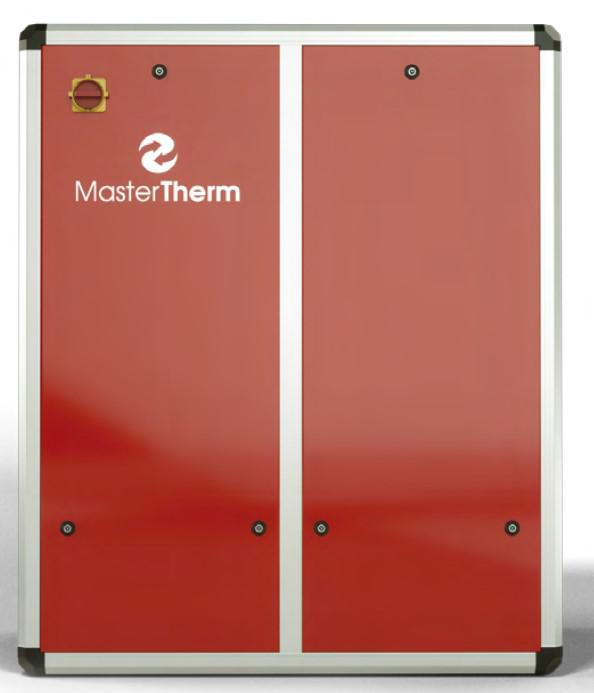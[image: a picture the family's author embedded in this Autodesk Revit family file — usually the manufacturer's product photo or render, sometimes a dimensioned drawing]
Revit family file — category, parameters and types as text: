
# Revit family: AQ-ZHX_ENG-RFA-2022
name_source: partatom
category: Mechanické zařízení
units: mm (PartAtom-declared; Revit-internal decimal feet)

## family parameters
Bod výpočtu místnosti = Ne
Kóta kulaté spojky = Použít průměr
Nadpis OmniClass = Climate Control (HVAC)
Ořezat dutým tvarem při načtení = Ne
Sdílené = Ne
Typ dílu = Normální
Vždy vertikální = Ano
Zachovat orientaci poznámky = Ne
Založené na pracovní rovině = Ne
Číslo OmniClass = 23.75.00.00

## types (5) — shared parameters
CI_condenser – inlet = 5/4'' (OD)
CO_condenser – outlet = 5/4'' (OD)
Desuperheater – inlet/outlet = not in unit
EI_evaporator – inlet = 5/4'' (OD)
EO_evaporator – outlet = 5/4'' (OD)
MT_CI diameter = 32 mm  [stored 0.104987 ft]
MT_CO diameter = 32 mm  [stored 0.104987 ft]
MT_EC1 offset_X = 25 mm  [stored 0.082021 ft]
MT_EC1 offset_Y = 90 mm  [stored 0.295276 ft]
MT_EC2 offset_X = 25 mm  [stored 0.082021 ft]
MT_EC2 offset_Y = 60 mm  [stored 0.19685 ft]
MT_EC3 offset_X = 25 mm  [stored 0.082021 ft]
MT_EC3 offset_Y = 30 mm  [stored 0.0984252 ft]
MT_EC4 offset_Y = 90 mm  [stored 0.295276 ft]
MT_EC5 offset_Y = 60 mm  [stored 0.19685 ft]
MT_EC6 offset_Y = 30 mm  [stored 0.0984252 ft]
MT_EC6_YES = Ano
MT_EI diameter = 32 mm  [stored 0.104987 ft]
MT_EO diameter = 32 mm  [stored 0.104987 ft]
MT_active power = 0 W
MT_angle length_Y = 596 mm  [stored 1.95538 ft]
MT_angle length_Z = 1080 mm
MT_angle offset = 60 mm  [stored 0.19685 ft]
MT_apparent power = 0 VA
MT_case depth = 716 mm  [stored 2.34908 ft]
MT_case height = 1200 mm
MT_case mat = MT_rgb161-42-32
MT_clearance back = 200 mm  [stored 0.656168 ft]
MT_clearance front = 600 mm
MT_clearance left = 400 mm  [stored 1.31234 ft]
MT_clearance right = 400 mm  [stored 1.31234 ft]
MT_clearance top = 1800 mm
MT_cover front_Y = 1120 mm
MT_cover side_X = 636 mm  [stored 2.08661 ft]
MT_cover side_Y = 1120 mm
MT_cover top_Y = 636 mm  [stored 2.08661 ft]
MT_desuperheater_YES = Ne
MT_frequency (Hz) = 50 Hz
MT_ground height = 30 mm  [stored 0.0984252 ft]
MT_pipe connector mat = MT_RGB-130-130-130
MT_pipe connector_Y = 120 mm  [stored 0.393701 ft]
MT_pipe mat = MT_angle-corner
MT_voltage (V) = 400 V
Popis = High-temperature heat pump
URL = https://www.mastertherm.eu
Výrobce = Master Therm
zero-valued in all types: Cena, MT_CosPhi, MT_desuperheater diameter, Výchozí výška

## per-type parameters (varying)
| type | El. connection | Komentáře k typům | MT_CI offset_X | MT_CO offset_X | MT_EC4 offset_X | MT_EC5 offset_X | MT_EC6 offset_X | MT_EI offset_X | MT_EO offset_X | MT_TYPE | MT_angle length_X | MT_case width | MT_center lock offset_H | MT_cover front_X | MT_cover top_X | MT_desuperheater offset_X | MT_double case_YES | MT_hmotnost (kg) | MT_lock offset_H | MT_logo offset_H | MT_max. current – compressor (A) | MT_pipe connector offset | MT_pipe connector_X | MT_power switch offset_H |
| AQ75ZHX | 4xPG16; 8xPG13.5 | COMPRESSOR: Scroll; 2900 rpm; charge of POE oil – 3.38 l; LRC – 174 (90); max. op. current – 35 A; EVAPORATOR: PHE; AISI316; water flow (W/W) – 3.04 kg/s; min. flow – 1.52 kg/s; temp. difference – 5 K; int. volume – 7.9 l; pump ext. head – 6.0 m; pump motor – 1100 W; CONDENSER: PHE; AISI316; water flow – 1.83 kg/s; min. flow – 1.83 kg/s; temp. difference – 10 K; int. volume – 6.9 l; pump ext. head – 5.0 m; pump motor – 310 W; REFRIGERANT CIRCUIT: R134a (5.0 kg); AUX. HEATER (optional); CONTROLS: controller – pCO5; EEV – yes; water probe – yes; SHW probe/output – yes (2x); mixing probe/output – yes; outdoor probe – yes; dynamic set point – yes; refrigerant probe – 2xPT; POWER SUPPLY: 3x400 V; 50 Hz; max. current – 40 A; max. current, incl. aux. heater – on demand; DIMENSIONS: hot water, brine – 5/4", 5/4" (OD); 120x101x72 cm; 400 kg; LIMITS: max. water overpress. – 0.25 MPa; max. refr. overpress. – 2.9 MPa; brine min./max.: 0/45 °C; water min./max.: 20/80 °C | 73 mm  [stored 0.239501 ft] | 173 mm  [stored 0.567585 ft] | 907 mm | 907 mm | 907 mm | 759 mm  [stored 2.49016 ft] | 859 mm  [stored 2.81824 ft] | 75 | 892 mm  [stored 2.92651 ft] | 1012 mm | 263 mm  [stored 0.862861 ft] | 932 mm | 932 mm | 466 mm  [stored 1.52887 ft] | Ano | 400 | 100 mm  [stored 0.328084 ft] | 263 mm  [stored 0.862861 ft] | 40 A | 972 mm | 932 mm | 175 mm  [stored 0.574147 ft] |
| AQ60ZHX | 2xPG21; 2xPG16; 4xPG13.5 | COMPRESSOR: Scroll; 3000 rpm; charge of POE oil – 3.38 l; LRC – 140; max. op. current – 27 A; EVAPORATOR: PHE; AISI316; water flow (W/W) – 2.54 kg/s; min. flow – 1.27 kg/s; temp. difference – 5 K; int. volume – 5.1 l; pump ext. head – 5.0 m; pump motor – 620 W; CONDENSER: PHE; AISI316; water flow – 1.52 kg/s; min. flow – 1.52 kg/s; temp. difference – 10 K; int. volume – 4.1 l; pump ext. head – 7.0 m; pump motor – 310 W; REFRIGERANT CIRCUIT: R134a (4.4 kg); AUX. HEATER (optional); CONTROLS: controller – pCO5; EEV – 1; water probe – yes; SHW probe/output – yes (2x); mixing probe/output – yes; outdoor probe – yes; dynamic set point – yes; refrigerant probe – 2xPT; POWER SUPPLY: 3x400 V; 50 Hz; max. current – 32 A; max. current, incl. aux. heater – on demand; DIMENSIONS: hot water, brine – 5/4", 5/4" (OD); 120x72x72 cm; 230 kg; LIMITS: max. water overpress. – 0.6 MPa; max. refr. overpress. – 4.2 MPa; brine min./max.: 0/50 °C; water min./max.: 20/80 °C | 93 mm  [stored 0.305118 ft] | 243 mm  [stored 0.797244 ft] | 608 mm  [stored 1.99475 ft] | 608 mm  [stored 1.99475 ft] | 608 mm  [stored 1.99475 ft] | 543 mm  [stored 1.7815 ft] | 393 mm  [stored 1.28937 ft] | 60 | 596 mm  [stored 1.95538 ft] | 716 mm  [stored 2.34908 ft] | 358 mm  [stored 1.17454 ft] | 636 mm  [stored 2.08661 ft] | 636 mm  [stored 2.08661 ft] | 318 mm  [stored 1.04331 ft] | Ne | 230 | 150 mm | 358 mm  [stored 1.17454 ft] | 32 A | 676 mm | 636 mm  [stored 2.08661 ft] | 250 mm  [stored 0.82021 ft] |
| AQ100.2ZHX | 4xPG16; 8xPG13.5 | COMPRESSOR: 2xScroll; 2900 rpm; charge of POE oil – 2x3.38 l; LRC – 139 (81); max. op. current – 2x21 A; EVAPORATOR: PHE; AISI316; water flow (W/W) – 3.38 kg/s; min. flow – 1.93 kg/s; temp. difference – 5 K; int. volume – 7.9 l; pump ext. head – 4.0 m; pump motor – 1100 W; CONDENSER: PHE; AISI316; water flow – 2.07 kg/s; min. flow – 2.07 kg/s; temp. difference – 10 K; int. volume – 6.9 l; pump ext. head – 3.0 m; pump motor – 310 W; REFRIGERANT CIRCUIT: R134a (10.0 kg); AUX. HEATER (optional); CONTROLS: controller – pCO5; EEV – yes; water probe – yes; SHW probe/output – yes (2x); mixing probe/output – yes; outdoor probe – yes; dynamic set point – yes; refrigerant probe – 2xPT; POWER SUPPLY: 3x400 V; 50 Hz; max. current – 50 A; max. current, incl. aux. heater – on demand; DIMENSIONS: hot water, brine – 5/4", 5/4" (OD); 120x101x72 cm; 400 kg; LIMITS: max. water overpress. – 0.25 MPa; max. refr. overpress. – 2.8 MPa; brine min./max.: 0/45 °C; water min./max.: 20/80 °C | 73 mm  [stored 0.239501 ft] | 173 mm  [stored 0.567585 ft] | 907 mm | 907 mm | 907 mm | 759 mm  [stored 2.49016 ft] | 859 mm  [stored 2.81824 ft] | 100 | 892 mm  [stored 2.92651 ft] | 1012 mm | 263 mm  [stored 0.862861 ft] | 932 mm | 932 mm | 466 mm  [stored 1.52887 ft] | Ano | 400 | 100 mm  [stored 0.328084 ft] | 263 mm  [stored 0.862861 ft] | 50 A | 972 mm | 932 mm | 175 mm  [stored 0.574147 ft] |
| AQ40ZHX | 2xPG21; 2xPG16; 4xPG13.5 | COMPRESSOR: Scroll; 3000 rpm; charge of POE oil – 2.65 l; LRC – 95 (45); max. op. current – 17 A; EVAPORATOR: PHE; AISI316; water flow (W/W) – 2.08 kg/s; min. flow – 1.04 kg/s; temp. difference – 5 K; int. volume – 5.1 l; pump ext. head – 5.0 m; pump motor – 310 W; CONDENSER: PHE; AISI316; water flow – 1.19 kg/s; min. flow – 1.19 kg/s; temp. difference – 10 K; int. volume – 4.1 l; pump ext. head – 8.0 m; pump motor – 310 W; REFRIGERANT CIRCUIT: R134a (4.2 kg); AUX. HEATER (optional); CONTROLS: controller – pCO5; EEV – 1; water probe – yes; SHW probe/output – yes (2x); mixing probe/output – yes; outdoor probe – yes; dynamic set point – yes; refrigerant probe – 2xPT; POWER SUPPLY: 3x400 V; 50 Hz; max. current – 20 A; max. current, incl. aux. heater – on demand; DIMENSIONS: hot water, brine – 5/4", 5/4" (OD); 120x53x72 cm; 230 kg; LIMITS: max. water overpress. – 0.6 MPa; max. refr. overpress. – 2.9 MPa; brine min./max.: 10/45 °C; water min./max.: 30/82 °C | 73 mm  [stored 0.239501 ft] | 173 mm  [stored 0.567585 ft] | 421 mm  [stored 1.38123 ft] | 421 mm  [stored 1.38123 ft] | 421 mm  [stored 1.38123 ft] | 373 mm  [stored 1.22375 ft] | 273 mm  [stored 0.895669 ft] | 40 | 406 mm  [stored 1.33202 ft] | 526 mm  [stored 1.72572 ft] | 263 mm  [stored 0.862861 ft] | 446 mm  [stored 1.46325 ft] | 446 mm  [stored 1.46325 ft] | 223 mm  [stored 0.731627 ft] | Ne | 230 | 100 mm  [stored 0.328084 ft] | 263 mm  [stored 0.862861 ft] | 20 A | 486 mm | 446 mm  [stored 1.46325 ft] | 175 mm  [stored 0.574147 ft] |
| AQ50ZHX | 2xPG21; 2xPG16; 4xPG13.5 | COMPRESSOR: Scroll; 3000 rpm; charge of POE oil – 3.38 l; LRC – 118 (60); max. op. current – 21 A; EVAPORATOR: PHE; AISI316; water flow (W/W) – 2.13 kg/s; min. flow – 1.06 kg/s; temp. difference – 5 K; int. volume – 5.1 l; pump ext. head – 4.0 m; pump motor – 310 W; CONDENSER: PHE; AISI316; water flow – 1.25 kg/s; min. flow – 1.25 kg/s; temp. difference – 10 K; int. volume – 4.1 l; pump ext. head – 10.0 m; pump motor – 310 W; REFRIGERANT CIRCUIT: R134a (5.0 kg); AUX. HEATER (optional); CONTROLS: controller – pCO5; EEV – 1; water probe – yes; SHW probe/output – yes (2x); mixing probe/output – yes; outdoor probe – yes; dynamic set point – yes; refrigerant probe – 2xPT; POWER SUPPLY: 3x400 V; 50 Hz; max. current – 25 A; max. current, incl. aux. heater – on demand; DIMENSIONS: hot water, brine – 5/4", 5/4" (OD); 120x72x72 cm; 230 kg; LIMITS: max. water overpress. – 0.6 MPa; max. refr. overpress. – 4.2 MPa; brine min./max.: 0/45 °C; water min./max.: 20/80 °C | 93 mm  [stored 0.305118 ft] | 243 mm  [stored 0.797244 ft] | 608 mm  [stored 1.99475 ft] | 608 mm  [stored 1.99475 ft] | 608 mm  [stored 1.99475 ft] | 543 mm  [stored 1.7815 ft] | 393 mm  [stored 1.28937 ft] | 50 | 596 mm  [stored 1.95538 ft] | 716 mm  [stored 2.34908 ft] | 358 mm  [stored 1.17454 ft] | 636 mm  [stored 2.08661 ft] | 636 mm  [stored 2.08661 ft] | 318 mm  [stored 1.04331 ft] | Ne | 230 | 150 mm | 358 mm  [stored 1.17454 ft] | 25 A | 676 mm | 636 mm  [stored 2.08661 ft] | 250 mm  [stored 0.82021 ft] |

note: column(s) folded — value = type name in every type: Model

note: [stored X ft] marks values corroborated as IEEE doubles in the binary element streams (Revit-internal decimal feet)
